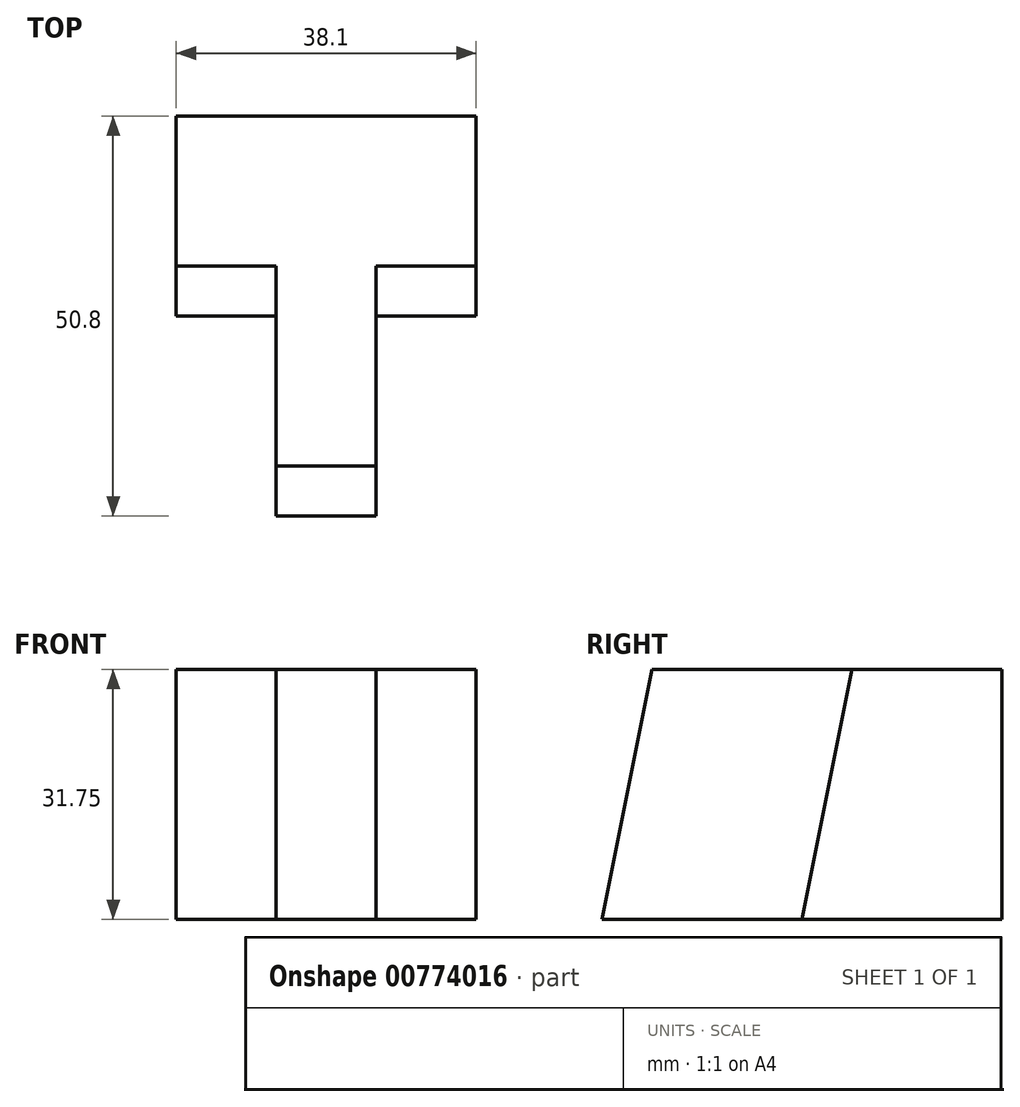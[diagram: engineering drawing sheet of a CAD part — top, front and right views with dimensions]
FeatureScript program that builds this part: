
annotation { "Feature Type Name" : "Feature", "Feature Type Description" : "" }
export const myFeature = defineFeature(function(context is Context, id is Id, definition is map)
    precondition{}
    {
        {
            var Q0;
            Q0=qCreatedBy(makeId("Front.planeOp"),FACE);
            var sketch = newSketch(context, id + "F0", { "sketchPlane" : qUnion([Q0])});
            skLineSegment(sketch, "E0", {"start": v(0, 0) * mm, "end": v(38.1, 0) * mm});
            skLineSegment(sketch, "E1", {"start": v(38.1, 0) * mm, "end": v(38.1, 31.75) * mm});
            skLineSegment(sketch, "E2", {"start": v(38.1, 31.75) * mm, "end": v(0, 31.75) * mm});
            skLineSegment(sketch, "E3", {"start": v(0, 31.75) * mm, "end": v(0, 0) * mm});
            skSolve(sketch);
        }
        {
            var Q0;
            Q0=makeQuery(id+"F0.imprint","IMPRINT",FACE,{"disambiguationData":[TD([[makeQuery(id+"F0.imprint","IMPRINT",EDGE,{"derivedFrom":sQuery(id+"F0.wireOp",EDGE,"E0")}),1.0]])]});
            extrude(context, id + "F1", {"entities" : qUnion([Q0]), "depth" : 44.45 * mm, "offsetDistance" : 25.4 * mm});
        }
        {
            var Q0;
            Q0=makeQuery(id+"F1.opExtrude","CAP_FACE",FACE,{"disambiguationData":[OSD([sQuery(id+"F0.wireOp",EDGE,"E0"),sQuery(id+"F0.wireOp",EDGE,"E1"),sQuery(id+"F0.wireOp",EDGE,"E2"),sQuery(id+"F0.wireOp",EDGE,"E3")])],"isStart":false});
            var sketch = newSketch(context, id + "F2", { "sketchPlane" : qUnion([Q0])});
            skLineSegment(sketch, "E4", {"start": v(38.1, 0) * mm, "end": v(25.4, 0) * mm});
            skLineSegment(sketch, "E5", {"start": v(0, 0) * mm, "end": v(12.7, 0) * mm});
            skLineSegment(sketch, "E6", {"start": v(12.7, 0) * mm, "end": v(12.7, 31.75) * mm});
            skLineSegment(sketch, "E7", {"start": v(25.4, 0) * mm, "end": v(25.4, 31.75) * mm});
            skSolve(sketch);
        }
        {
            var Q0;
            Q0=makeQuery(id+"F2.imprint","IMPRINT",FACE,{"disambiguationData":[TD([[makeQuery(id+"F2.imprint","IMPRINT",EDGE,{"derivedFrom":sQuery(id+"F2.wireOp",EDGE,"E4")}),1.0]])]});
            var Q1;
            Q1=makeQuery(id+"F2.imprint","IMPRINT",FACE,{"disambiguationData":[TD([[makeQuery(id+"F2.imprint","IMPRINT",EDGE,{"derivedFrom":sQuery(id+"F2.wireOp",EDGE,"E5")}),1.0]])]});
            extrude(context, id + "F3", {"entities" : qUnion([Q0, Q1]), "operationType" : NewBodyOperationType.REMOVE, "oppositeDirection" : true, "depth" : 19.05 * mm, "offsetDistance" : 25.4 * mm});
        }
        {
            var Q0;
            Q0=makeQuery(id+"F1.opExtrude","SWEPT_FACE",FACE,{"disambiguationData":[OSD([sQuery(id+"F0.wireOp",EDGE,"E1")])]});
            var sketch = newSketch(context, id + "F4", { "sketchPlane" : qUnion([Q0])});
            skLineSegment(sketch, "E8", {"start": v(0, 31.75) * mm, "end": v(-19.05, 31.75) * mm});
            skLineSegment(sketch, "E9", {"start": v(-19.05, 31.75) * mm, "end": v(-25.4, 0) * mm});
            skSolve(sketch);
        }
        {
            var Q0;
            {var subQ0=sQuery(id+"F4.wireOp",EDGE,"E9");Q0=makeQuery(id+"F4.imprint","IMPRINT",FACE,{"disambiguationData":[TD([[makeQuery(id+"F4.imprint","IMPRINT",EDGE,{"derivedFrom":subQ0}),-1.0]])]});}
            extrude(context, id + "F5", {"entities" : qUnion([Q0]), "operationType" : NewBodyOperationType.REMOVE, "oppositeDirection" : true, "depth" : 12.7 * mm, "offsetDistance" : 25.4 * mm});
        }
        {
            var Q0;
            Q0=makeQuery(id+"F1.opExtrude","SWEPT_FACE",FACE,{"disambiguationData":[OSD([sQuery(id+"F0.wireOp",EDGE,"E3")])]});
            var sketch = newSketch(context, id + "F6", { "sketchPlane" : qUnion([Q0])});
            skLineSegment(sketch, "E10", {"start": v(25.4, 31.75) * mm, "end": v(19.05, 31.75) * mm});
            skLineSegment(sketch, "E11", {"start": v(19.05, 31.75) * mm, "end": v(25.4, 0) * mm});
            skSolve(sketch);
        }
        {
            var Q0;
            Q0=makeQuery(id+"F6.imprint","IMPRINT",FACE,{"disambiguationData":[TD([[makeQuery(id+"F6.imprint","IMPRINT",EDGE,{"derivedFrom":sQuery(id+"F6.wireOp",EDGE,"E10")}),1.0]])]});
            extrude(context, id + "F7", {"entities" : qUnion([Q0]), "operationType" : NewBodyOperationType.REMOVE, "oppositeDirection" : true, "depth" : 12.7 * mm, "offsetDistance" : 25.4 * mm});
        }
        {
            var Q0;
            Q0 = qSketchRegion(id + "FxYeSnAqkcOBXm4_1", true);
            var Q1;
            Q1=makeQuery(id+"F1.opExtrude","CAP_FACE",FACE,{"disambiguationData":[OSD([sQuery(id+"F0.wireOp",EDGE,"E0"),sQuery(id+"F0.wireOp",EDGE,"E1"),sQuery(id+"F0.wireOp",EDGE,"E2"),sQuery(id+"F0.wireOp",EDGE,"E3")])],"isStart":false});
            extrude(context, id + "F8", {"entities" : qUnion([Q0, Q1]), "operationType" : NewBodyOperationType.ADD, "depth" : 6.35 * mm, "offsetDistance" : 25.4 * mm});
        }
        {
            var Q0;
            {var subQ0=sQuery(id+"F2.wireOp",EDGE,"E7");Q0=makeQuery(id+"F8.boolean.opBoolean","MERGE",FACE,{"derivedFrom":[makeQuery(id+"F5.boolean.opBoolean","MERGE",FACE,{"derivedFrom":[makeQuery(id+"F3.boolean.opBoolean","COPY",FACE,{"derivedFrom":makeQuery(id+"F3.opExtrude","SWEPT_FACE",FACE,{"disambiguationData":[OSD([subQ0])]})}),makeQuery(id+"F5.opExtrude","CAP_FACE",FACE,{"disambiguationData":[OSD([sQuery(id+"F0.wireOp",EDGE,"E1"),sQuery(id+"F0.wireOp",EDGE,"E2"),sQuery(id+"F4.wireOp",EDGE,"E9")])],"isStart":false})]}),makeQuery(id+"F8.opExtrude","SWEPT_FACE",FACE,{"disambiguationData":[OSD([subQ0])]})]});}
            var sketch = newSketch(context, id + "F9", { "sketchPlane" : qUnion([Q0])});
            skLineSegment(sketch, "E12", {"start": v(-19.05, 31.75) * mm, "end": v(-44.45, 31.75) * mm});
            skLineSegment(sketch, "E13", {"start": v(-44.45, 31.75) * mm, "end": v(-50.8, 0) * mm});
            skSolve(sketch);
        }
        {
            var Q0;
            {var subQ0=sQuery(id+"F9.wireOp",EDGE,"E13");Q0=makeQuery(id+"F9.imprint","IMPRINT",FACE,{"disambiguationData":[TD([[makeQuery(id+"F9.imprint","IMPRINT",EDGE,{"derivedFrom":subQ0}),-1.0]])]});}
            extrude(context, id + "F10", {"entities" : qUnion([Q0]), "operationType" : NewBodyOperationType.REMOVE, "oppositeDirection" : true, "depth" : 25.4 * mm, "offsetDistance" : 25.4 * mm});
        }
    });
